# Revit family: Door-Exterior-Single-Quarter Glass
name_source: partatom
category: Doors
revit_build: Autodesk Revit LT 2017 (Build: 20161205_1400(x64)
units: mm (PartAtom-declared; Revit-internal decimal feet)

## family parameters
Always vertical = Yes
Cut with Voids When Loaded = No
Host = Wall
OmniClass Number = 23.30.10.14
OmniClass Title = Passage Doors by Material
Room Calculation Point = No
Shared = No

## types (2) — shared parameters
Analytic Construction = French door, wood frame with single glass
Assembly Code = B2030100
Bottom Rail = 9 1/2"
Door Handle Material = Aluminum
Frame Material = Cherry
Function = Exterior
Glazing = Glass
Heat Transfer Coefficient (U) = 0.935 BTU/(h·ft²·°F)
Height = 80"
HeightFeet = 6
HeightInches = 8
HeightReal = 6.666667
Lock Rail = 7 1/8"
Muntins Vert 3Lites = Yes
Panel Material = Cherry
Rough Height = 81"
Stiles = 4 3/4"
Thermal Resistance (R) = 1.0696 (h·ft²·°F)/BTU
Thickness = 1 3/8"
Threshold Material = Cherry
Top Rail = 4 3/4"
Trim Material = Cherry
Wall Closure = By host
zero-valued in all types: Solar Heat Gain Coefficient, Visual Light Transmittance

## per-type parameters (varying)
| type | Construction Type | Muntins Horz 2Lites | Muntins Horz 3Lites | Muntins Vert 2Lites | Rough Width | Width | WidthFeet | WidthInches | WidthReal |
| 36" x 80" | ENTRY | Yes | Yes | Yes | 38" | 36" | 3 | 0 | 3 |
| 32" x 80" | 3  LITE | No | No | No | 34" | 32" | 2 | 8 | 2.666667 |

## geometry (parser evidence)
native form markers: Blend x8, Sweep x11
no freeform markers — native parametric forms only
